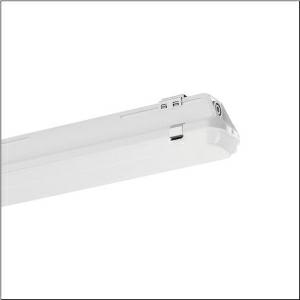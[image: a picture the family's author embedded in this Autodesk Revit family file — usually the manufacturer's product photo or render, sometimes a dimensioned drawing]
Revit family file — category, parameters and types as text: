
# Revit family: monsun_r__11_51fp107p460h_50c3
name_source: partatom
category: Lighting Fixtures
units: mm (PartAtom-declared; Revit-internal decimal feet)

## family parameters
Cut with Voids When Loaded = No
Host = Face
Light Source = No
Part Type = Normal
Room Calculation Point = No
Round Connector Dimension = Use Diameter
Shared = No

## types (1)
- Monsun® 11 (1 x LED, 5800 lm, 32.5 W, 4000K)
    Apparent Load = 33 VA
    CIE Flux Codes = 47 77 93 94 100
    Color Rendering = 80
    Color Temperature = 4000K
    Default Elevation = 1800 mm
    Description = Monsun® 11, damp-proof luminaire, chain hanger, primary optical cover: enclosure, of PMMA, light emission: direct distribution, primary light characteristic: symmetric, installation type: suspended mounting, surface-mounted, horizontal mounting, vertical mounting, LED, rated luminous flux: 5.800lm, luminous efficacy: 178lm/W, light colour: 840, colour temperature: 4000K, control gear: ON/OFF, with terminal, 3-pole, max. 2.5mm², mains connection: 220..240V, AC, 50/60Hz, rated input power: 33W, luminaire housing, of glass-fibre reinforced polyester, uncoated, bright grey, incl. chain hanger, length: 1.590mm, width: 90mm, height: 88mm, clip for enclosure, of stainless steel (V2A), ceiling mounting element, of stainless steel (V2A), chain hanger, of stainless steel (V2A), protection rating (complete): IP66, insulation class (complete): insulation class I (protective earthing), certification: CE, ENEC, VDE, UKCA, protection symbol: D, impact resistance: IK04, permissible operating ambient temperature: -35..+40°C, standard: EN 50419, EN 60598-2-1, no direct snow, no direct sun, no direct rain, for indoor or canopied outdoor use, corresponds to IFS (International Featured Standards) requirements for safety and quality in the food industry, contact your sales advisor before using the luminaires in applications with unclear chemical exposure, large temperature fluctuations or condensation-forming humidity, LABS conformity tested according to VDMA 24364:2018-05, packaging unit: 1 piece
    Height = 89 mm
    Lamp = 1 x LED
    Lamp Light Flux = 5800 lm
    Lamp Power = 32.5 W
    Lamp count = 1
    Length = 1590 mm
    Luminous efficacy = 178 lm/W
    Manufacturer = Siteco
    ModVariant = No
    Model = 51FP107P460H
    Mounting Place = Ceiling
    Mounting Type = Surface mounted
    Number of Poles = 1
    OnlyDefault = Yes
    Power Factor = 1
    Product Name = Monsun® 11
    Product group = damp-proof luminaire
    ProductGroupID = 301
    Protection Class = Protection class I
    Protection Degree = IP 66
    RLX_Detail_Level = 1
    RLX_Emergency_Light_Flux = 0 lm
    RLX_Emergency_Type = 0
    RLX_Emergency_Type_DB = No
    RlxData = <blob elided: 88677 chars, md5=4d8fa7e2>
    Socket = socket
    Standby Power = 0 W
    System Light Flux = 5800 lm
    System Power = 33 W
    Type Comments = Product without accessories
    Type Image = l_1349237.jpg
    URL = http://relux.com
    VarID = ---
    Voltage = 0 V
    Weight = 0.00 kg
    Width = 90 mm

## geometry (parser evidence)
native form markers: Blend x4, Sweep x13
no freeform markers — native parametric forms only
